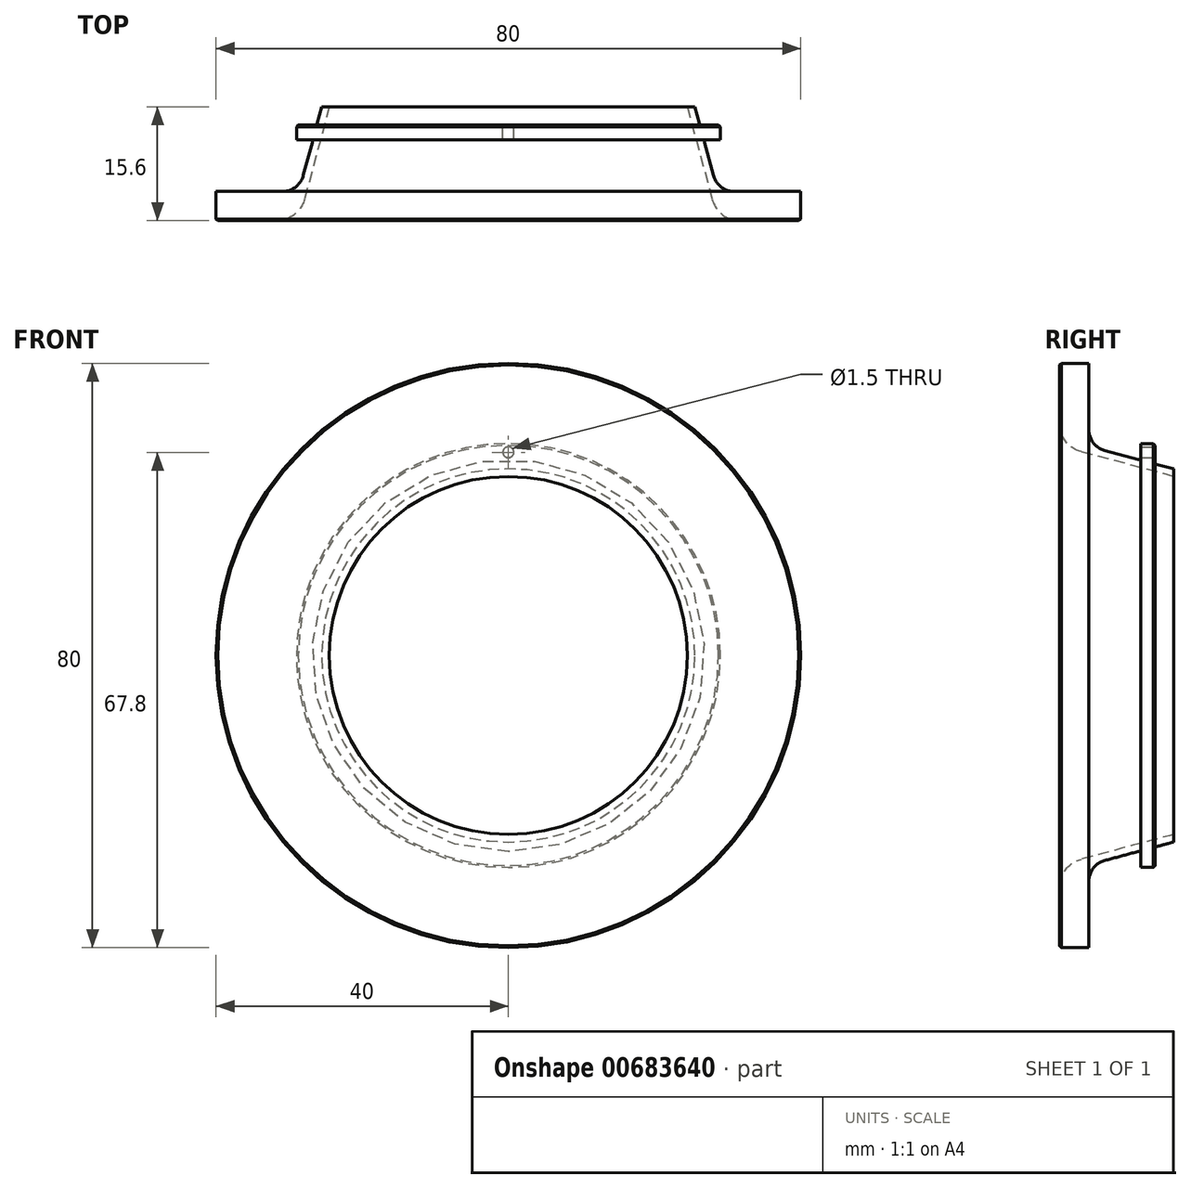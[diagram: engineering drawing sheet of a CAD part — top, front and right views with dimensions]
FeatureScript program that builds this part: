
annotation { "Feature Type Name" : "Feature", "Feature Type Description" : "" }
export const myFeature = defineFeature(function(context is Context, id is Id, definition is map)
    precondition{}
    {
        {
            var Q0;
            Q0=qCreatedBy(makeId("Right.planeOp"),FACE);
            var sketch = newSketch(context, id + "F0", { "sketchPlane" : qUnion([Q0])});
            skLineSegment(sketch, "E0", {"start": v(-34.36, 0) * mm, "end": v(35.83, 0) * mm, "construction": true});
            skLineSegment(sketch, "E1", {"start": v(0, 39.75) * mm, "end": v(0, 31.75) * mm});
            skLineSegment(sketch, "E2", {"start": v(2.96, 27.89) * mm, "end": v(15.6, 24.5) * mm});
            skLineSegment(sketch, "E3", {"start": v(15.6, 24.5) * mm, "end": v(15.6, 25.54) * mm});
            skLineSegment(sketch, "E4", {"start": v(4, 40) * mm, "end": v(0.25, 40) * mm});
            skPoint(sketch, "E5.visualSharp", {"position": v(0, 28.68) * mm});
            skArc(sketch, "E5.filletArc", {"start": v(0, 31.75) * mm, "mid": v(0.83, 29.31) * mm, "end": v(2.96, 27.89) * mm});
            skLineSegment(sketch, "E6", {"start": v(0, 39.75) * mm, "end": v(0.25, 40) * mm});
            skPoint(sketch, "E7.orphan", {"position": v(0, 40) * mm});
            skLineSegment(sketch, "E8", {"start": v(15.6, 25.54) * mm, "end": v(13.32, 26.15) * mm});
            skLineSegment(sketch, "E9", {"start": v(4, 40) * mm, "end": v(4, 30.95) * mm});
            skLineSegment(sketch, "E10", {"start": v(12.85, 29) * mm, "end": v(11.1, 29) * mm});
            skLineSegment(sketch, "E11", {"start": v(11.1, 29) * mm, "end": v(11.1, 27.13) * mm});
            skLineSegment(sketch, "E12", {"start": v(13.1, 28.75) * mm, "end": v(13.1, 26.44) * mm});
            skLineSegment(sketch, "E13.trimOffspring", {"start": v(10.72, 26.84) * mm, "end": v(6.22, 28.05) * mm});
            skPoint(sketch, "E14.visualSharp", {"position": v(4, 28.64) * mm});
            skArc(sketch, "E14.filletArc", {"start": v(4, 30.95) * mm, "mid": v(4.62, 29.12) * mm, "end": v(6.22, 28.05) * mm});
            skPoint(sketch, "E15.visualSharp", {"position": v(11.1, 26.74) * mm});
            skArc(sketch, "E15.filletArc", {"start": v(10.72, 26.84) * mm, "mid": v(10.98, 26.9) * mm, "end": v(11.1, 27.13) * mm});
            skPoint(sketch, "E16.visualSharp", {"position": v(13.1, 26.2) * mm});
            skArc(sketch, "E16.filletArc", {"start": v(13.1, 26.44) * mm, "mid": v(13.16, 26.25) * mm, "end": v(13.32, 26.15) * mm});
            skLineSegment(sketch, "E17", {"start": v(12.85, 29) * mm, "end": v(13.1, 28.75) * mm});
            skPoint(sketch, "E18.orphan", {"position": v(13.1, 29) * mm});
            skSolve(sketch);
        }
        {
            var Q0;
            Q0=makeQuery(id+"F0.imprint","IMPRINT",FACE,{"disambiguationData":[TD([[makeQuery(id+"F0.imprint","IMPRINT",EDGE,{"derivedFrom":sQuery(id+"F0.wireOp",EDGE,"E1")}),1.0]])]});
            var Q1;
            Q1=sQuery(id+"F0.wireOp",EDGE,"E0");
            revolve(context, id + "F1", {"entities" : qUnion([Q0]), "axis" : qUnion([Q1]), "revolveType" : RevolveType.FULL});
        }
        {
            var Q0;
            Q0=makeQuery(id+"F1.opRevolve","SWEPT_FACE",FACE,{"disambiguationData":[OSD([sQuery(id+"F0.wireOp",EDGE,"E12")])]});
            var sketch = newSketch(context, id + "F2", { "sketchPlane" : qUnion([Q0])});
            skPoint(sketch, "E19", {"position": v(0, 27.8) * mm});
            skSolve(sketch);
        }
        {
            var Q0;
            Q0=sQuery(id+"F2.wireOp",VERTEX,"E19");
            var Q1;
            Q1=makeQuery(id+"F1.opRevolve","SWEPT_BODY",BODY,{"disambiguationData":[OSD([sQuery(id+"F0.wireOp",EDGE,"E1"),sQuery(id+"F0.wireOp",EDGE,"E2"),sQuery(id+"F0.wireOp",EDGE,"E3"),sQuery(id+"F0.wireOp",EDGE,"m7h4Ksze-jS88-FNtZ-Gc6C-LBZPbLpovlct"),sQuery(id+"F0.wireOp",EDGE,"czNFdaMc-sNaQ-h8XT-ZtVP-1jvIfX261BBY"),sQuery(id+"F0.wireOp",EDGE,"Bgvr0M2L-423R-kNmR-wSWg-F4xc2lxdQmay"),sQuery(id+"F0.wireOp",EDGE,"LOR0JQpn-WoUJ-UY4W-KfCq-AlZ0gRI963YP"),sQuery(id+"F0.wireOp",EDGE,"tqs3Cv8j-7rW0-iXYB-VeVx-CvU7x2y5Id5C"),sQuery(id+"F0.wireOp",EDGE,"QTppXvfw-hEvl-xwbG-bFPc-3APoA2olr8CE"),sQuery(id+"F0.wireOp",EDGE,"E4"),sQuery(id+"F0.wireOp",EDGE,"E5.filletArc"),sQuery(id+"F0.wireOp",EDGE,"9eb34949-871e-41fb-8c6e-4924b103c45d.filletArc")])]});
            hole(context, id + "F3", {"style" : HoleStyle.SIMPLE, "endStyle" : HoleEndStyle.BLIND, "holeDiameter" : 1.5 * mm, "majorDiameter" : 5 * mm, "holeDepth" : 2.2 * mm, "isTappedThrough" : true, "tappedDepth" : 12 * mm, "tapClearance" : 3, "locations" : qUnion([Q0]), "scope" : qUnion([Q1])});
        }
    });
